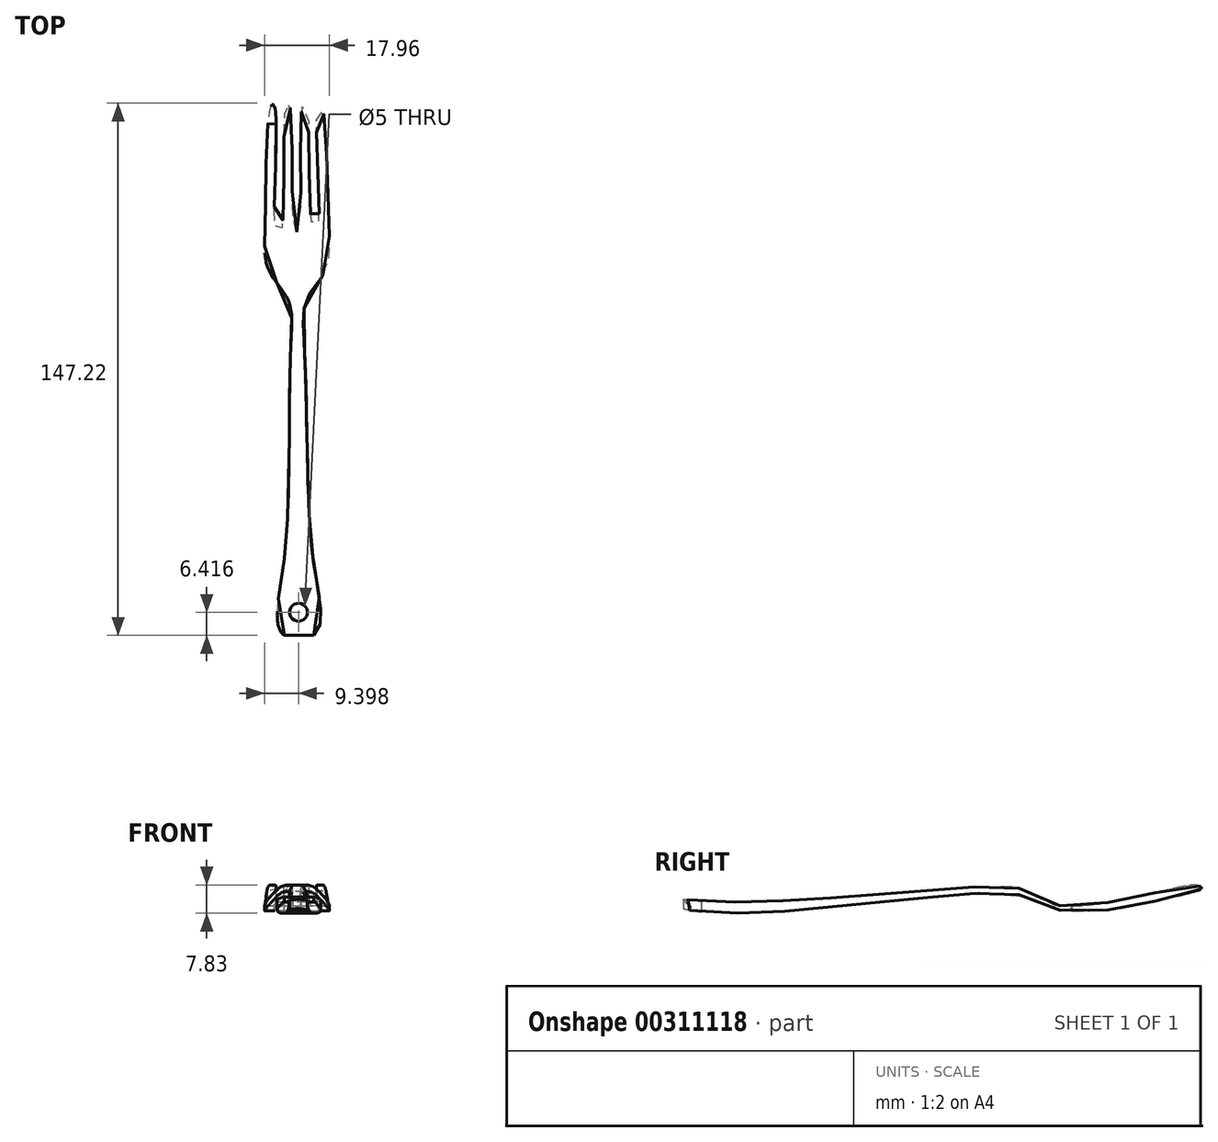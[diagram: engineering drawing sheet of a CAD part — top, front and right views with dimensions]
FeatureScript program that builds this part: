
annotation { "Feature Type Name" : "Feature", "Feature Type Description" : "" }
export const myFeature = defineFeature(function(context is Context, id is Id, definition is map)
    precondition{}
    {
        {
            var Q0;
            Q0=qCreatedBy(makeId("Top.planeOp"),FACE);
            var sketch = newSketch(context, id + "F0", { "sketchPlane" : qUnion([Q0])});
            skLineSegment(sketch, "E0.bottom", {"start": v(50, -90) * mm, "end": v(-50, -90) * mm});
            skLineSegment(sketch, "E0.top", {"start": v(50, 90) * mm, "end": v(-50, 90) * mm});
            skLineSegment(sketch, "E0.left", {"start": v(50, -90) * mm, "end": v(50, 90) * mm});
            skLineSegment(sketch, "E0.right", {"start": v(-50, -90) * mm, "end": v(-50, 90) * mm});
            skPoint(sketch, "E0.middle", {"position": v(0, 0) * mm});
            skSolve(sketch);
        }
        {
            var Q0;
            Q0 = qSketchRegion(id + "F0", true);
            extrude(context, id + "F1", {"entities" : qUnion([Q0]), "depth" : 25 * mm});
        }
        {
            var Q0;
            Q0=makeQuery(id+"F1.opExtrude","CAP_FACE",FACE,{"disambiguationData":[OSD([sQuery(id+"F0.wireOp",EDGE,"E0.bottom"),sQuery(id+"F0.wireOp",EDGE,"E0.top"),sQuery(id+"F0.wireOp",EDGE,"E0.left"),sQuery(id+"F0.wireOp",EDGE,"E0.right")])],"isStart":false});
            var sketch = newSketch(context, id + "F2", { "sketchPlane" : qUnion([Q0])});
            skFitSpline(sketch, "E1", {"points": [v(2.1, 40.97) * mm, v(2.83, 41.82) * mm, v(3.55, 75.36) * mm, v(4.4, 76.58) * mm, v(5.13, 74.75) * mm, v(6.35, 41.7) * mm, v(7.2, 40.72) * mm, v(8.05, 42.19) * mm, v(7.68, 74.63) * mm, v(8.54, 76.34) * mm, v(9.55, 73.15) * mm, v(10.93, 43.26) * mm, v(9.9, 30.34) * mm, v(4.77, 22.25) * mm, v(4.22, 8.07) * mm, v(5.96, -44.04) * mm, v(8.34, -60.48) * mm, v(7.84, -69.45) * mm, v(2.73, -72.37) * mm], "startDerivative": vector(44.58, 9.27) * mm, "endDerivative": vector(-161.88, -49.21) * mm});
            skFitSpline(sketch, "E2.MirrorCS", {"points": [v(2.11, 40.97) * mm, v(1.37, 41.81) * mm, v(0.27, 75.34) * mm, v(-0.6, 76.55) * mm, v(-1.3, 74.72) * mm, v(-2.15, 41.65) * mm, v(-3, 40.66) * mm, v(-3.86, 42.12) * mm, v(-3.85, 74.57) * mm, v(-4.72, 76.27) * mm, v(-5.7, 73.06) * mm, v(-6.75, 43.16) * mm, v(-5.58, 30.26) * mm, v(-0.36, 22.23) * mm, v(0.35, 8.05) * mm, v(-0.81, -44.07) * mm, v(-3, -60.54) * mm, v(-2.41, -69.5) * mm, v(2.73, -72.37) * mm], "startDerivative": vector(-44.68, 8.78) * mm, "endDerivative": vector(162.42, -47.42) * mm});
            skSolve(sketch);
        }
        {
            var Q0;
            Q0=makeQuery(id+"F1.opExtrude","SWEPT_FACE",FACE,{"disambiguationData":[OSD([sQuery(id+"F0.wireOp",EDGE,"E0.right")])]});
            var sketch = newSketch(context, id + "F3", { "sketchPlane" : qUnion([Q0])});
            skFitSpline(sketch, "E3", {"points": [v(-76.13, 15.3) * mm, v(-63.25, 13.2) * mm, v(-34.36, 10.25) * mm, v(-25.9, 14.72) * mm, v(-19.48, 15.3) * mm, v(30.44, 11.62) * mm, v(57.85, 10.86) * mm, v(69.64, 11.93) * mm, v(70.43, 12.06) * mm, v(70.58, 11.17) * mm, v(66.8, 8.97) * mm, v(50.63, 7.67) * mm, v(25.05, 9.46) * mm, v(-23.1, 13.62) * mm, v(-26.36, 12.68) * mm, v(-31.63, 9.43) * mm, v(-38.43, 8.42) * mm, v(-47.59, 8.44) * mm, v(-57.48, 9.67) * mm, v(-74.94, 13.83) * mm, v(-76.64, 14.58) * mm, v(-76.13, 15.3) * mm]});
            skSolve(sketch);
        }
        {
            var Q0;
            Q0 = qSketchRegion(id + "F3", true);
            extrude(context, id + "F4", {"entities" : qUnion([Q0]), "operationType" : NewBodyOperationType.INTERSECT, "oppositeDirection" : true, "depth" : 200 * mm});
        }
        {
            var Q0;
            Q0 = qSketchRegion(id + "F2", true);
            extrude(context, id + "F5", {"entities" : qUnion([Q0]), "operationType" : NewBodyOperationType.INTERSECT, "oppositeDirection" : true, "depth" : 30 * mm});
        }
        {
            var Q0;
            Q0=qCreatedBy(makeId("Top.planeOp"),FACE);
            var sketch = newSketch(context, id + "F6", { "sketchPlane" : qUnion([Q0])});
            skLineSegment(sketch, "E4", {"start": v(-1.64, -70.6) * mm, "end": v(6.72, -70.6) * mm, "construction": true});
            skLineSegment(sketch, "E5", {"start": v(2.54, -70.6) * mm, "end": v(2.54, -64.21) * mm, "construction": true});
            skCircle(sketch, "E6", {"center": v(2.54, -64.21) * mm, "radius": 2.5 * mm});
            skSolve(sketch);
        }
        {
            var Q0;
            Q0 = qSketchRegion(id + "F6", true);
            extrude(context, id + "F7", {"entities" : qUnion([Q0]), "operationType" : NewBodyOperationType.REMOVE, "depth" : 30.3 * mm});
        }
    });
